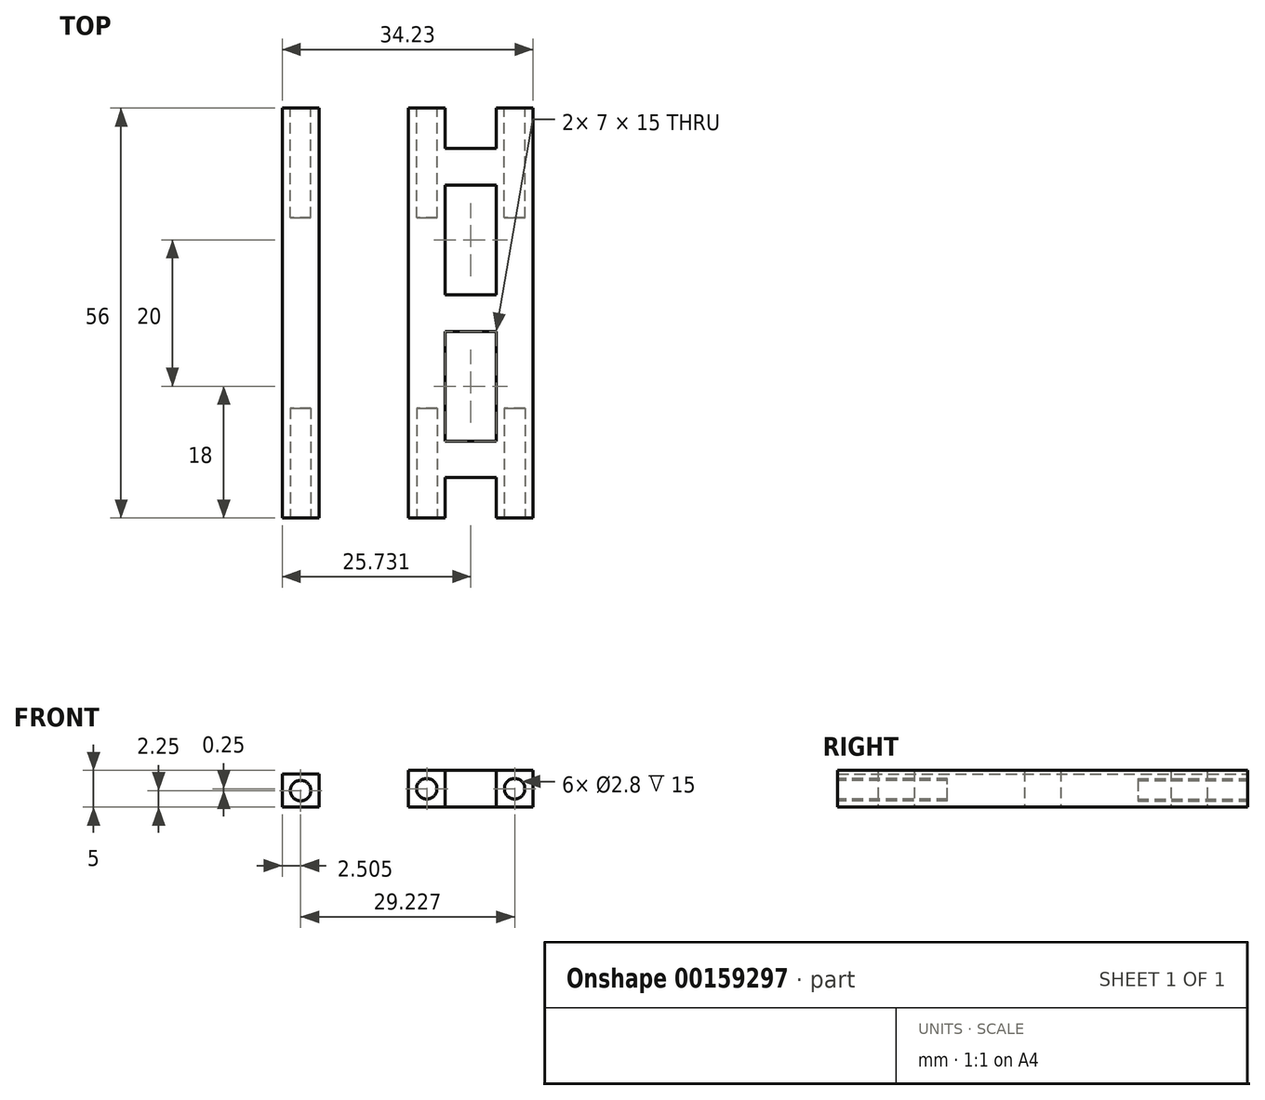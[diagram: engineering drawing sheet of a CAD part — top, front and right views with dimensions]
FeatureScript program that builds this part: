
annotation { "Feature Type Name" : "Feature", "Feature Type Description" : "" }
export const myFeature = defineFeature(function(context is Context, id is Id, definition is map)
    precondition{}
    {
        {
            var Q0;
            Q0=qCreatedBy(makeId("Front.planeOp"),FACE);
            var sketch = newSketch(context, id + "F0", { "sketchPlane" : qUnion([Q0])});
            skLineSegment(sketch, "E0.bottom", {"start": v(-9.8, 0) * mm, "end": v(-4.8, 0) * mm});
            skLineSegment(sketch, "E0.top", {"start": v(-9.8, 4.5) * mm, "end": v(-4.8, 4.5) * mm});
            skLineSegment(sketch, "E0.left", {"start": v(-9.8, 0) * mm, "end": v(-9.8, 4.5) * mm});
            skLineSegment(sketch, "E0.right", {"start": v(-4.8, 0) * mm, "end": v(-4.8, 4.5) * mm});
            skSolve(sketch);
        }
        {
            var Q0;
            Q0 = qSketchRegion(id + "F0", true);
            extrude(context, id + "F1", {"entities" : qUnion([Q0]), "depth" : 56 * mm});
        }
        {
            var Q0;
            Q0=makeQuery(id+"F1.opExtrude","CAP_FACE",FACE,{"disambiguationData":[OSD([sQuery(id+"F0.wireOp",EDGE,"E0.bottom"),sQuery(id+"F0.wireOp",EDGE,"E0.top"),sQuery(id+"F0.wireOp",EDGE,"E0.left"),sQuery(id+"F0.wireOp",EDGE,"E0.right")])],"isStart":false});
            var sketch = newSketch(context, id + "F2", { "sketchPlane" : qUnion([Q0])});
            skCircle(sketch, "E1", {"center": v(-7.3, 2.25) * mm, "radius": 1.4 * mm});
            skPoint(sketch, "E1.centerSnap0", {"position": v(-7.3, 4.5) * mm});
            skPoint(sketch, "E1.centerSnap1", {"position": v(-9.8, 2.25) * mm});
            skSolve(sketch);
        }
        {
            var Q0;
            Q0 = qSketchRegion(id + "F2", true);
            extrude(context, id + "F3", {"entities" : qUnion([Q0]), "operationType" : NewBodyOperationType.REMOVE, "oppositeDirection" : true, "depth" : 15 * mm});
        }
        {
            var Q0;
            Q0=makeQuery(id+"F1.opExtrude","CAP_FACE",FACE,{"disambiguationData":[OSD([sQuery(id+"F0.wireOp",EDGE,"E0.bottom"),sQuery(id+"F0.wireOp",EDGE,"E0.top"),sQuery(id+"F0.wireOp",EDGE,"E0.left"),sQuery(id+"F0.wireOp",EDGE,"E0.right")])],"isStart":true});
            var sketch = newSketch(context, id + "F4", { "sketchPlane" : qUnion([Q0])});
            skCircle(sketch, "E2", {"center": v(7.3, 2.25) * mm, "radius": 1.4 * mm});
            skPoint(sketch, "E2.centerSnap0", {"position": v(7.3, 4.5) * mm});
            skPoint(sketch, "E2.centerSnap1", {"position": v(4.8, 2.25) * mm});
            skSolve(sketch);
        }
        {
            var Q0;
            Q0 = qSketchRegion(id + "F4", true);
            extrude(context, id + "F5", {"entities" : qUnion([Q0]), "operationType" : NewBodyOperationType.REMOVE, "oppositeDirection" : true, "depth" : 15 * mm});
        }
        {
            var Q0;
            Q0=qCreatedBy(makeId("Top.planeOp"),FACE);
            var sketch = newSketch(context, id + "F6", { "sketchPlane" : qUnion([Q0])});
            skLineSegment(sketch, "E3.bottom", {"start": v(7.43, 0) * mm, "end": v(12.43, 0) * mm});
            skLineSegment(sketch, "E3.top", {"start": v(7.43, -56) * mm, "end": v(12.43, -56) * mm});
            skLineSegment(sketch, "E3.left", {"start": v(7.43, 0) * mm, "end": v(7.43, -56) * mm});
            skLineSegment(sketch, "E3.right", {"start": v(12.43, 0) * mm, "end": v(12.43, -5.5) * mm});
            skLineSegment(sketch, "E4.bottom", {"start": v(19.43, 0) * mm, "end": v(24.43, 0) * mm});
            skLineSegment(sketch, "E4.top", {"start": v(19.43, -56) * mm, "end": v(24.43, -56) * mm});
            skLineSegment(sketch, "E4.left", {"start": v(19.43, 0) * mm, "end": v(19.43, -5.5) * mm});
            skLineSegment(sketch, "E4.right", {"start": v(24.43, 0) * mm, "end": v(24.43, -56) * mm});
            skLineSegment(sketch, "E5.bottom", {"start": v(12.43, -5.5) * mm, "end": v(19.43, -5.5) * mm});
            skLineSegment(sketch, "E5.top", {"start": v(12.43, -10.5) * mm, "end": v(19.43, -10.5) * mm});
            skLineSegment(sketch, "E6.bottom", {"start": v(12.43, -25.5) * mm, "end": v(19.43, -25.5) * mm});
            skLineSegment(sketch, "E6.top", {"start": v(12.43, -30.5) * mm, "end": v(19.43, -30.5) * mm});
            skLineSegment(sketch, "E7.bottom", {"start": v(12.43, -45.5) * mm, "end": v(19.43, -45.5) * mm});
            skLineSegment(sketch, "E7.top", {"start": v(12.43, -50.5) * mm, "end": v(19.43, -50.5) * mm});
            skLineSegment(sketch, "E8.trimOffspring", {"start": v(12.43, -10.5) * mm, "end": v(12.43, -25.5) * mm});
            skLineSegment(sketch, "E9.trimOffspring", {"start": v(19.43, -10.5) * mm, "end": v(19.43, -25.5) * mm});
            skLineSegment(sketch, "E10.trimOffspring", {"start": v(19.43, -30.5) * mm, "end": v(19.43, -45.5) * mm});
            skLineSegment(sketch, "E11.trimOffspring", {"start": v(12.43, -30.5) * mm, "end": v(12.43, -45.5) * mm});
            skLineSegment(sketch, "E12.trimOffspring", {"start": v(12.43, -50.5) * mm, "end": v(12.43, -56) * mm});
            skLineSegment(sketch, "E13.trimOffspring", {"start": v(19.43, -50.5) * mm, "end": v(19.43, -56) * mm});
            skSolve(sketch);
        }
        {
            var Q0;
            Q0 = qSketchRegion(id + "F6", true);
            extrude(context, id + "F7", {"entities" : qUnion([Q0]), "depth" : 5 * mm});
        }
        {
            var Q0;
            Q0=makeQuery(id+"F7.opExtrude","SWEPT_FACE",FACE,{"disambiguationData":[OSD([sQuery(id+"F6.wireOp",EDGE,"E3.top")])]});
            var sketch = newSketch(context, id + "F8", { "sketchPlane" : qUnion([Q0])});
            skCircle(sketch, "E14", {"center": v(9.93, 2.5) * mm, "radius": 1.4 * mm});
            skPoint(sketch, "E14.centerSnap0", {"position": v(9.93, 5) * mm});
            skPoint(sketch, "E14.centerSnap1", {"position": v(7.43, 2.5) * mm});
            skCircle(sketch, "E15", {"center": v(21.93, 2.5) * mm, "radius": 1.4 * mm});
            skSolve(sketch);
        }
        {
            var Q0;
            Q0=makeQuery(id+"F7.opExtrude","SWEPT_FACE",FACE,{"disambiguationData":[OSD([sQuery(id+"F6.wireOp",EDGE,"E4.bottom")])]});
            var sketch = newSketch(context, id + "F9", { "sketchPlane" : qUnion([Q0])});
            skCircle(sketch, "E16", {"center": v(-21.93, 2.5) * mm, "radius": 1.4 * mm});
            skCircle(sketch, "E17", {"center": v(-9.93, 2.5) * mm, "radius": 1.4 * mm});
            skSolve(sketch);
        }
        {
            var Q0;
            Q0 = qSketchRegion(id + "F8", true);
            extrude(context, id + "F10", {"entities" : qUnion([Q0]), "operationType" : NewBodyOperationType.REMOVE, "oppositeDirection" : true, "depth" : 15 * mm});
        }
        {
            var Q0;
            Q0 = qSketchRegion(id + "F9", true);
            extrude(context, id + "F11", {"entities" : qUnion([Q0]), "operationType" : NewBodyOperationType.REMOVE, "oppositeDirection" : true, "depth" : 15 * mm});
        }
    });
